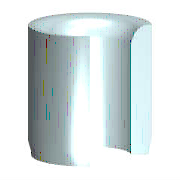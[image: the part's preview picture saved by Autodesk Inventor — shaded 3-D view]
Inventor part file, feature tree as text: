
AUTODESK INVENTOR PART (.ipt)
format: ipt  version: 2023.3 (Build 273359000, 359)  size: 153,088 bytes
history: native  units: mm (DEFAULTED — no unit token found)
features: hole x2, other x1, sketch x1
ambient origin geometry x8: Origin, YZ Plane, XZ Plane, XY Plane, X Axis, Y Axis, Z Axis, Center Point
bodies: Solid1 (feature_tree)
feature tree (4):
  other  "Körper"
  sketch  "Skizze2"  dims[d0=6.0mm d1=3.0mm d2=12.0mm d3=90.0deg d6=1.0mm d7=15.0deg d9=0.0mm d11=1.0mm d12=0.0mm d13=1.0mm d14=6.0mm d15=0.5mm d16=6.0mm d17=4.0mm d18=2.0mm d19=90.0deg d20=12.0mm d21=0.0mm d23=1.0mm d24=6.0mm d25=4.0mm d26=2.0mm d27=90.0deg d28=8.0mm d29=0.0mm d30=1.5mm]
  hole  "Bohrung1"  [1 undecoded]
  hole  "Bohrung2"  [1 undecoded]
note: 2 required parameter values undecoded (feature->parameter linkage not recoverable at this tier; creation-order binding heuristic only, values carry confidence <= 0.55)
